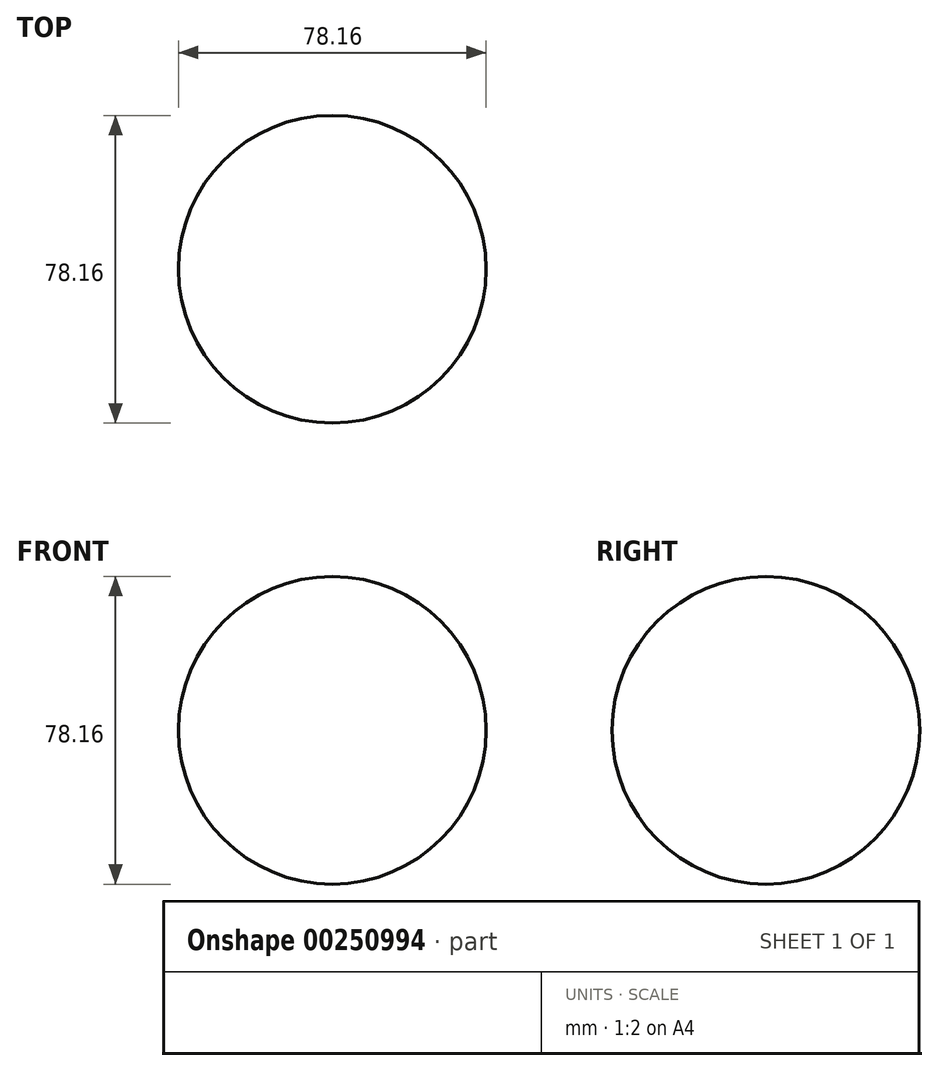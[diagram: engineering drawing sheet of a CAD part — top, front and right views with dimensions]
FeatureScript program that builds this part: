
annotation { "Feature Type Name" : "Feature", "Feature Type Description" : "" }
export const myFeature = defineFeature(function(context is Context, id is Id, definition is map)
    precondition{}
    {
        {
            var Q0;
            Q0=qCreatedBy(makeId("Front.planeOp"),FACE);
            var sketch = newSketch(context, id + "F0", { "sketchPlane" : qUnion([Q0])});
            skLineSegment(sketch, "E0", {"start": v(0, 0) * mm, "end": v(0, 78.16) * mm});
            skArc(sketch, "E1", {"start": v(0, 78.16) * mm, "mid": v(-39.08, 39.08) * mm, "end": v(0, 0) * mm});
            skSolve(sketch);
        }
        {
            var Q0;
            Q0 = qSketchRegion(id + "F0", true);
            var Q1;
            Q1=sQuery(id+"F0.wireOp",EDGE,"E0");
            revolve(context, id + "F1", {"entities" : qUnion([Q0]), "axis" : qUnion([Q1]), "revolveType" : RevolveType.FULL});
        }
    });
